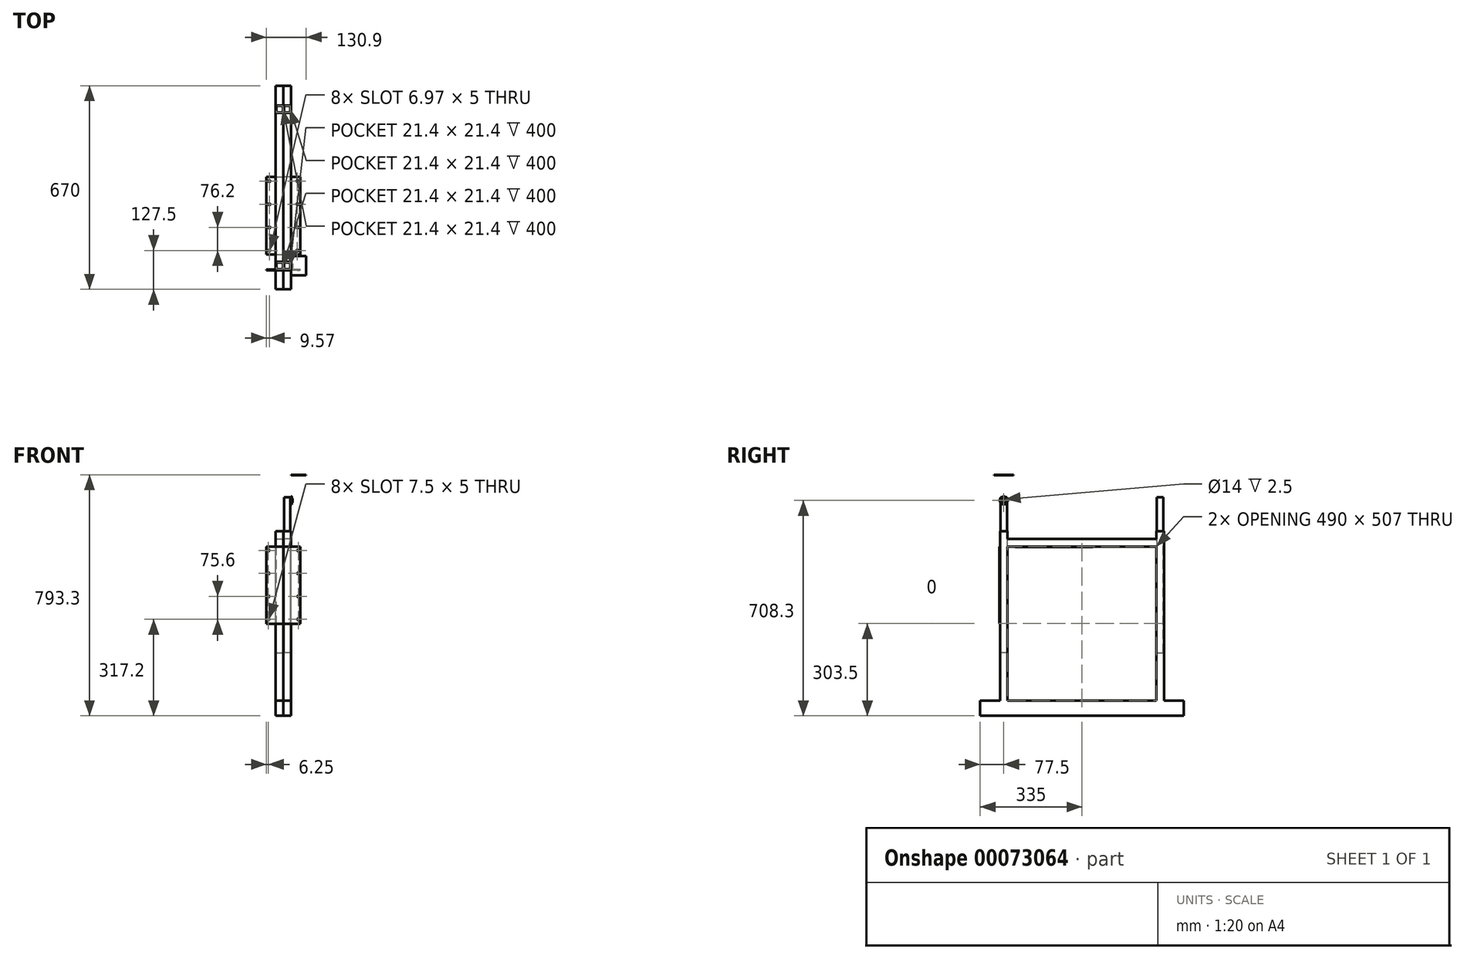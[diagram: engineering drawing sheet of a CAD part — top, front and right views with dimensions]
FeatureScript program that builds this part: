
annotation { "Feature Type Name" : "Feature", "Feature Type Description" : "" }
export const myFeature = defineFeature(function(context is Context, id is Id, definition is map)
    precondition{}
    {
        {
            var Q0;
            Q0=qCreatedBy(makeId("Right.planeOp"),FACE);
            var sketch = newSketch(context, id + "F0", { "sketchPlane" : qUnion([Q0])});
            skLineSegment(sketch, "E0", {"start": v(-335, 0) * mm, "end": v(335, 0) * mm});
            skLineSegment(sketch, "E1.0", {"start": v(-335, 50) * mm, "end": v(335, 50) * mm});
            skLineSegment(sketch, "E2", {"start": v(-335, 50) * mm, "end": v(-335, 0) * mm});
            skLineSegment(sketch, "E3", {"start": v(335, 50) * mm, "end": v(335, 0) * mm});
            skLineSegment(sketch, "E4", {"start": v(270, 50) * mm, "end": v(270, 607) * mm});
            skLineSegment(sketch, "E5.0", {"start": v(245, 50) * mm, "end": v(245, 607) * mm});
            skLineSegment(sketch, "E6", {"start": v(245, 607) * mm, "end": v(270, 607) * mm});
            skLineSegment(sketch, "E7", {"start": v(0, 0) * mm, "end": v(0, 674.81) * mm, "construction": true});
            skPoint(sketch, "E7.endSnap0", {"position": v(0, 50) * mm});
            skLineSegment(sketch, "E8.MirrorCS", {"start": v(-245, 607) * mm, "end": v(-270, 607) * mm});
            skLineSegment(sketch, "E9.MirrorCS", {"start": v(-270, 50) * mm, "end": v(-270, 607) * mm});
            skLineSegment(sketch, "E10.MirrorCS", {"start": v(-245, 50) * mm, "end": v(-245, 607) * mm});
            skLineSegment(sketch, "E11", {"start": v(-245, 557) * mm, "end": v(245, 557) * mm});
            skLineSegment(sketch, "E12.0", {"start": v(-245, 582) * mm, "end": v(245, 582) * mm});
            skLineSegment(sketch, "E13", {"start": v(-220, 557) * mm, "end": v(-220, 555) * mm});
            skLineSegment(sketch, "E14", {"start": v(-220, 555) * mm, "end": v(35, 555) * mm});
            skLineSegment(sketch, "E15", {"start": v(35, 555) * mm, "end": v(35, 557) * mm});
            skLineSegment(sketch, "E16", {"start": v(-270, 557) * mm, "end": v(-272, 557) * mm});
            skLineSegment(sketch, "E17", {"start": v(-272, 557) * mm, "end": v(-272, 302) * mm});
            skLineSegment(sketch, "E18", {"start": v(-272, 302) * mm, "end": v(-270, 302) * mm});
            skSolve(sketch);
        }
        {
            var Q0;
            Q0=makeQuery(id+"F0.imprint","IMPRINT",FACE,{"disambiguationData":[TD([[makeQuery(id+"F0.imprint","IMPRINT",EDGE,{"derivedFrom":sQuery(id+"F0.wireOp",EDGE,"E0")}),1.0]])]});
            var Q1;
            {var subQ5=sQuery(id+"F0.wireOp",EDGE,"E4");Q1=makeQuery(id+"F0.imprint","IMPRINT",FACE,{"disambiguationData":[TD([[makeQuery(id+"F0.imprint","IMPRINT",EDGE,{"derivedFrom":subQ5}),1.0]])]});}
            var Q2;
            {var subQ8=sQuery(id+"F0.wireOp",EDGE,"E8.MirrorCS");Q2=makeQuery(id+"F0.imprint","IMPRINT",FACE,{"disambiguationData":[TD([[makeQuery(id+"F0.imprint","IMPRINT",EDGE,{"derivedFrom":subQ8}),1.0]])]});}
            var Q3;
            {var subQ5=sQuery(id+"F0.wireOp",EDGE,"E12.0");Q3=makeQuery(id+"F0.imprint","IMPRINT",FACE,{"disambiguationData":[TD([[makeQuery(id+"F0.imprint","IMPRINT",EDGE,{"derivedFrom":subQ5}),-1.0]])]});}
            extrude(context, id + "F1", {"entities" : qUnion([Q0, Q1, Q2, Q3]), "depth" : 25 * mm});
        }
        {
            var Q0;
            {var subQ0=sQuery(id+"F0.wireOp",EDGE,"E13");Q0=makeQuery(id+"F0.imprint","IMPRINT",FACE,{"disambiguationData":[TD([[makeQuery(id+"F0.imprint","IMPRINT",EDGE,{"derivedFrom":subQ0}),1.0]])]});}
            var Q1;
            {var subQ0=sQuery(id+"F0.wireOp",EDGE,"E16");Q1=makeQuery(id+"F0.imprint","IMPRINT",FACE,{"disambiguationData":[TD([[makeQuery(id+"F0.imprint","IMPRINT",EDGE,{"derivedFrom":subQ0}),1.0]])]});}
            extrude(context, id + "F2", {"entities" : qUnion([Q0, Q1]), "operationType" : NewBodyOperationType.ADD, "depth" : 55.7 * mm});
        }
        {
            var Q0;
            Q0=makeQuery(id+"F2.opExtrude","SWEPT_FACE",FACE,{"disambiguationData":[OSD([sQuery(id+"F0.wireOp",EDGE,"E11")])]});
            var sketch = newSketch(context, id + "F3", { "sketchPlane" : qUnion([Q0])});
            skArc(sketch, "E19", {"start": v(46.7, -209.96) * mm, "mid": v(49.64, -207.65) * mm, "end": v(47, -205) * mm});
            skArc(sketch, "E20", {"start": v(45.15, -205) * mm, "mid": v(42.64, -207.53) * mm, "end": v(45.2, -210) * mm});
            skLineSegment(sketch, "E21", {"start": v(47.7, -209.94) * mm, "end": v(45.2, -210) * mm});
            skLineSegment(sketch, "E22", {"start": v(47, -205) * mm, "end": v(45.15, -205) * mm});
            skArc(sketch, "E23.0.1.0", {"start": v(46.7, -133.76) * mm, "mid": v(49.64, -131.45) * mm, "end": v(47, -128.8) * mm});
            skArc(sketch, "E23.0.1.1", {"start": v(45.15, -128.8) * mm, "mid": v(42.64, -131.33) * mm, "end": v(45.2, -133.8) * mm});
            skLineSegment(sketch, "E23.0.1.2", {"start": v(47.7, -133.74) * mm, "end": v(45.2, -133.8) * mm});
            skLineSegment(sketch, "E23.0.1.3", {"start": v(47, -128.8) * mm, "end": v(45.15, -128.8) * mm});
            skArc(sketch, "E23.0.2.0", {"start": v(46.7, -57.56) * mm, "mid": v(49.64, -55.25) * mm, "end": v(47, -52.6) * mm});
            skArc(sketch, "E23.0.2.1", {"start": v(45.15, -52.6) * mm, "mid": v(42.64, -55.13) * mm, "end": v(45.2, -57.6) * mm});
            skLineSegment(sketch, "E23.0.2.2", {"start": v(47.7, -57.54) * mm, "end": v(45.2, -57.6) * mm});
            skLineSegment(sketch, "E23.0.2.3", {"start": v(47, -52.6) * mm, "end": v(45.15, -52.6) * mm});
            skArc(sketch, "E23.0.3.0", {"start": v(46.7, 18.64) * mm, "mid": v(49.64, 20.95) * mm, "end": v(47, 23.6) * mm});
            skArc(sketch, "E23.0.3.1", {"start": v(45.15, 23.6) * mm, "mid": v(42.64, 21.07) * mm, "end": v(45.2, 18.6) * mm});
            skLineSegment(sketch, "E23.0.3.2", {"start": v(47.7, 18.66) * mm, "end": v(45.2, 18.6) * mm});
            skLineSegment(sketch, "E23.0.3.3", {"start": v(47, 23.6) * mm, "end": v(45.15, 23.6) * mm});
            skLineSegment(sketch, "E23.direction1", {"start": v(46.7, -209.96) * mm, "end": v(37.88, -209.96) * mm, "construction": true});
            skLineSegment(sketch, "E23.direction2", {"start": v(46.7, -209.96) * mm, "end": v(46.7, -133.76) * mm, "construction": true});
            skSolve(sketch);
        }
        {
            var Q0;
            {var subQ3=sQuery(id+"F3.wireOp",EDGE,"E20");Q0=makeQuery(id+"F3.imprint","IMPRINT",FACE,{"disambiguationData":[TD([[makeQuery(id+"F3.imprint","IMPRINT",EDGE,{"derivedFrom":subQ3}),1.0]])]});}
            var Q1;
            {var subQ3=sQuery(id+"F3.wireOp",EDGE,"E23.0.1.1");Q1=makeQuery(id+"F3.imprint","IMPRINT",FACE,{"disambiguationData":[TD([[makeQuery(id+"F3.imprint","IMPRINT",EDGE,{"derivedFrom":subQ3}),1.0]])]});}
            var Q2;
            {var subQ3=sQuery(id+"F3.wireOp",EDGE,"E23.0.2.1");Q2=makeQuery(id+"F3.imprint","IMPRINT",FACE,{"disambiguationData":[TD([[makeQuery(id+"F3.imprint","IMPRINT",EDGE,{"derivedFrom":subQ3}),1.0]])]});}
            var Q3;
            {var subQ3=sQuery(id+"F3.wireOp",EDGE,"E23.0.3.1");Q3=makeQuery(id+"F3.imprint","IMPRINT",FACE,{"disambiguationData":[TD([[makeQuery(id+"F3.imprint","IMPRINT",EDGE,{"derivedFrom":subQ3}),1.0]])]});}
            extrude(context, id + "F4", {"entities" : qUnion([Q0, Q1, Q2, Q3]), "operationType" : NewBodyOperationType.REMOVE, "oppositeDirection" : true, "depth" : 5 * mm});
        }
        {
            var Q0;
            Q0=makeQuery(id+"F2.opExtrude","SWEPT_FACE",FACE,{"disambiguationData":[OSD([sQuery(id+"F0.wireOp",EDGE,"E17")])]});
            var sketch = newSketch(context, id + "F5", { "sketchPlane" : qUnion([Q0])});
            skArc(sketch, "E24", {"start": v(50.7, 541.5) * mm, "mid": v(53.2, 544) * mm, "end": v(50.7, 546.5) * mm});
            skArc(sketch, "E25", {"start": v(48.28, 546.5) * mm, "mid": v(45.7, 544.04) * mm, "end": v(48.2, 541.5) * mm});
            skLineSegment(sketch, "E26", {"start": v(48.28, 546.5) * mm, "end": v(50.7, 546.5) * mm});
            skLineSegment(sketch, "E27", {"start": v(48.2, 541.5) * mm, "end": v(50.7, 541.5) * mm});
            skArc(sketch, "E28.0.1.0", {"start": v(50.7, 465.9) * mm, "mid": v(53.2, 468.4) * mm, "end": v(50.7, 470.9) * mm});
            skArc(sketch, "E28.0.1.1", {"start": v(48.28, 470.9) * mm, "mid": v(45.7, 468.44) * mm, "end": v(48.2, 465.9) * mm});
            skLineSegment(sketch, "E28.0.1.2", {"start": v(48.28, 470.9) * mm, "end": v(50.7, 470.9) * mm});
            skLineSegment(sketch, "E28.0.1.3", {"start": v(48.2, 465.9) * mm, "end": v(50.7, 465.9) * mm});
            skArc(sketch, "E28.0.2.0", {"start": v(50.7, 390.3) * mm, "mid": v(53.2, 392.8) * mm, "end": v(50.7, 395.3) * mm});
            skArc(sketch, "E28.0.2.1", {"start": v(48.28, 395.3) * mm, "mid": v(45.7, 392.84) * mm, "end": v(48.2, 390.3) * mm});
            skLineSegment(sketch, "E28.0.2.2", {"start": v(48.28, 395.3) * mm, "end": v(50.7, 395.3) * mm});
            skLineSegment(sketch, "E28.0.2.3", {"start": v(48.2, 390.3) * mm, "end": v(50.7, 390.3) * mm});
            skArc(sketch, "E28.0.3.0", {"start": v(50.7, 314.7) * mm, "mid": v(53.2, 317.2) * mm, "end": v(50.7, 319.7) * mm});
            skArc(sketch, "E28.0.3.1", {"start": v(48.28, 319.7) * mm, "mid": v(45.7, 317.24) * mm, "end": v(48.2, 314.7) * mm});
            skLineSegment(sketch, "E28.0.3.2", {"start": v(48.28, 319.7) * mm, "end": v(50.7, 319.7) * mm});
            skLineSegment(sketch, "E28.0.3.3", {"start": v(48.2, 314.7) * mm, "end": v(50.7, 314.7) * mm});
            skLineSegment(sketch, "E28.direction1", {"start": v(50.7, 541.5) * mm, "end": v(71.48, 541.5) * mm, "construction": true});
            skLineSegment(sketch, "E28.direction2", {"start": v(50.7, 541.5) * mm, "end": v(50.7, 465.9) * mm, "construction": true});
            skSolve(sketch);
        }
        {
            var Q0;
            Q0 = qSketchRegion(id + "F5", true);
            extrude(context, id + "F6", {"entities" : qUnion([Q0]), "operationType" : NewBodyOperationType.REMOVE, "oppositeDirection" : true, "depth" : 28.93 * mm});
        }
        {
            var Q0;
            Q0=makeQuery(id+"F1.opExtrude","SWEPT_FACE",FACE,{"disambiguationData":[OSD([sQuery(id+"F0.wireOp",EDGE,"E8.MirrorCS")])]});
            var sketch = newSketch(context, id + "F7", { "sketchPlane" : qUnion([Q0])});
            skLineSegment(sketch, "E29.0", {"start": v(23.2, -246.8) * mm, "end": v(1.8, -246.8) * mm});
            skLineSegment(sketch, "E29.1", {"start": v(23.2, -246.8) * mm, "end": v(23.2, -268.2) * mm});
            skLineSegment(sketch, "E29.2", {"start": v(23.2, -268.2) * mm, "end": v(1.8, -268.2) * mm});
            skLineSegment(sketch, "E29.3", {"start": v(1.8, -246.8) * mm, "end": v(1.8, -268.2) * mm});
            skLineSegment(sketch, "E30.0", {"start": v(23.2, 268.2) * mm, "end": v(1.8, 268.2) * mm});
            skLineSegment(sketch, "E30.1", {"start": v(23.2, 246.8) * mm, "end": v(23.2, 268.2) * mm});
            skLineSegment(sketch, "E30.2", {"start": v(23.2, 246.8) * mm, "end": v(1.8, 246.8) * mm});
            skLineSegment(sketch, "E30.3", {"start": v(1.8, 246.8) * mm, "end": v(1.8, 268.2) * mm});
            skSolve(sketch);
        }
        {
            var Q0;
            Q0=makeQuery(id+"F7.imprint","IMPRINT",FACE,{"disambiguationData":[TD([[makeQuery(id+"F7.imprint","IMPRINT",EDGE,{"derivedFrom":sQuery(id+"F7.wireOp",EDGE,"E30.0")}),1.0]])]});
            var Q1;
            Q1=makeQuery(id+"F7.imprint","IMPRINT",FACE,{"disambiguationData":[TD([[makeQuery(id+"F7.imprint","IMPRINT",EDGE,{"derivedFrom":sQuery(id+"F7.wireOp",EDGE,"E29.0")}),1.0]])]});
            extrude(context, id + "F8", {"entities" : qUnion([Q0, Q1]), "operationType" : NewBodyOperationType.REMOVE, "oppositeDirection" : true, "depth" : 400 * mm});
        }
        {
            var Q0;
            Q0=makeQuery(id+"F8.boolean.opBoolean","COPY",FACE,{"derivedFrom":makeQuery(id+"F8.opExtrude","CAP_FACE",FACE,{"disambiguationData":[OSD([sQuery(id+"F7.wireOp",EDGE,"E29.0"),sQuery(id+"F7.wireOp",EDGE,"E29.1"),sQuery(id+"F7.wireOp",EDGE,"E29.2"),sQuery(id+"F7.wireOp",EDGE,"E29.3")])],"isStart":false})});
            extrude(context, id + "F9", {"entities" : qUnion([Q0]), "depth" : 512 * mm});
        }
        {
            var Q0;
            Q0=makeQuery(id+"F8.boolean.opBoolean","COPY",FACE,{"derivedFrom":makeQuery(id+"F8.opExtrude","CAP_FACE",FACE,{"disambiguationData":[OSD([sQuery(id+"F7.wireOp",EDGE,"E30.0"),sQuery(id+"F7.wireOp",EDGE,"E30.1"),sQuery(id+"F7.wireOp",EDGE,"E30.2"),sQuery(id+"F7.wireOp",EDGE,"E30.3")])],"isStart":false})});
            extrude(context, id + "F10", {"entities" : qUnion([Q0]), "depth" : 512 * mm});
        }
        {
            var Q0;
            Q0=makeQuery(id+"F9.opExtrude","SWEPT_FACE",FACE,{"disambiguationData":[OSD([sQuery(id+"F7.wireOp",EDGE,"E29.1")])]});
            var sketch = newSketch(context, id + "F11", { "sketchPlane" : qUnion([Q0])});
            skCircle(sketch, "E31", {"center": v(-257.5, 708.3) * mm, "radius": 10.7 * mm});
            skCircle(sketch, "E32", {"center": v(-257.5, 708.3) * mm, "radius": 7 * mm});
            skCircle(sketch, "E33", {"center": v(-257.5, 708.3) * mm, "radius": 13 * mm});
            skLineSegment(sketch, "E34", {"start": v(-257.5, 708.3) * mm, "end": v(-257.5, 796.5) * mm, "construction": true});
            skLineSegment(sketch, "E35", {"start": v(-257.5, 793.3) * mm, "end": v(-225.5, 793.3) * mm});
            skLineSegment(sketch, "E36", {"start": v(-225.5, 793.3) * mm, "end": v(-225.5, 738.3) * mm});
            skLineSegment(sketch, "E37", {"start": v(-225.5, 738.3) * mm, "end": v(-246.2, 701.88) * mm});
            skLineSegment(sketch, "E38.0", {"start": v(-257.5, 790.8) * mm, "end": v(-225.5, 790.8) * mm});
            skLineSegment(sketch, "E39.MirrorCS", {"start": v(-257.5, 790.8) * mm, "end": v(-289.5, 790.8) * mm});
            skLineSegment(sketch, "E40.MirrorCS", {"start": v(-257.5, 793.3) * mm, "end": v(-289.5, 793.3) * mm});
            skLineSegment(sketch, "E41.MirrorCS", {"start": v(-289.5, 793.3) * mm, "end": v(-289.5, 738.3) * mm});
            skLineSegment(sketch, "E42.MirrorCS", {"start": v(-289.5, 738.3) * mm, "end": v(-268.8, 701.88) * mm});
            skSolve(sketch);
        }
        {
            var Q0;
            Q0=makeQuery(id+"F11.imprint","IMPRINT",FACE,{"disambiguationData":[TD([[makeQuery(id+"F11.imprint","IMPRINT",EDGE,{"derivedFrom":sQuery(id+"F11.wireOp",EDGE,"E32")}),-1.0]])]});
            var Q1;
            Q1=sQuery(id+"F11.wireOp",EDGE,"E32");
            var Q2;
            Q2=sQuery(id+"F11.wireOp",EDGE,"E31");
            extrude(context, id + "F12", {"entities" : qUnion([Q0]), "surfaceEntities" : qUnion([Q1, Q2]), "depth" : 2.5 * mm});
        }
        {
            var Q0;
            Q0=makeQuery(id+"F11.imprint","IMPRINT",FACE,{"disambiguationData":[TD([[makeQuery(id+"F11.imprint","IMPRINT",EDGE,{"derivedFrom":sQuery(id+"F11.wireOp",EDGE,"E32")}),1.0]])]});
            extrude(context, id + "F13", {"entities" : qUnion([Q0]), "depth" : 7.5 * mm, "hasSecondDirection" : true, "secondDirectionOppositeDirection" : false, "secondDirectionDepth" : 2.5 * mm});
        }
        {
            var Q0;
            Q0=makeQuery(id+"F11.imprint","IMPRINT",FACE,{"disambiguationData":[TD([[makeQuery(id+"F11.imprint","IMPRINT",EDGE,{"derivedFrom":sQuery(id+"F11.wireOp",EDGE,"E32")}),-1.0]])]});
            var Q1;
            {var subQ0=sQuery(id+"F11.wireOp",EDGE,"E31");var subQ1=sQuery(id+"F7.wireOp",EDGE,"E29.1");var subQ2=makeQuery(id+"F9.opExtrude","SWEPT_EDGE",EDGE,{"disambiguationData":[OSD([sQuery(id+"F7.wireOp",EDGE,"E29.0"),subQ1])]});var subQ3=makeQuery(id+"F11.imprint","INTERSECT",VERTEX,{"derivedFrom":[subQ2,subQ0]});Q1=makeQuery(id+"F11.imprint","IMPRINT",FACE,{"disambiguationData":[TD([[makeQuery(id+"F11.imprint","IMPRINT",EDGE,{"disambiguationData":[TD([[subQ3,1.0]])],"derivedFrom":subQ0}),-1.0]])]});}
            var Q2;
            {var subQ0=sQuery(id+"F11.wireOp",EDGE,"E33");var subQ1=makeQuery(id+"F11.imprint","INTERSECT",VERTEX,{"derivedFrom":[subQ0,sQuery(id+"F11.wireOp",EDGE,"E42.MirrorCS")]});Q2=makeQuery(id+"F11.imprint","IMPRINT",FACE,{"disambiguationData":[TD([[makeQuery(id+"F11.imprint","IMPRINT",EDGE,{"disambiguationData":[TD([[subQ1,1.0]])],"derivedFrom":subQ0}),1.0]])]});}
            var Q3;
            {var subQ0=sQuery(id+"F11.wireOp",EDGE,"E33");var subQ1=makeQuery(id+"F11.imprint","INTERSECT",VERTEX,{"derivedFrom":[subQ0,sQuery(id+"F11.wireOp",EDGE,"E37")]});Q3=makeQuery(id+"F11.imprint","IMPRINT",FACE,{"disambiguationData":[TD([[makeQuery(id+"F11.imprint","IMPRINT",EDGE,{"disambiguationData":[TD([[subQ1,1.0]])],"derivedFrom":subQ0}),1.0]])]});}
            var Q4;
            {var subQ0=sQuery(id+"F11.wireOp",EDGE,"E31");var subQ1=sQuery(id+"F7.wireOp",EDGE,"E29.1");var subQ2=makeQuery(id+"F9.opExtrude","CAP_EDGE",EDGE,{"disambiguationData":[OSD([subQ1])],"isStart":false});var subQ3=makeQuery(id+"F11.imprint","INTERSECT",VERTEX,{"derivedFrom":[subQ2,subQ0]});Q4=makeQuery(id+"F11.imprint","IMPRINT",FACE,{"disambiguationData":[TD([[makeQuery(id+"F11.imprint","IMPRINT",EDGE,{"disambiguationData":[TD([[subQ3,1.0]])],"derivedFrom":subQ2}),1.0]])]});}
            var Q5;
            {var subQ0=sQuery(id+"F11.wireOp",EDGE,"E31");var subQ1=sQuery(id+"F7.wireOp",EDGE,"E29.1");var subQ2=makeQuery(id+"F9.opExtrude","CAP_EDGE",EDGE,{"disambiguationData":[OSD([subQ1])],"isStart":false});var subQ3=makeQuery(id+"F11.imprint","INTERSECT",VERTEX,{"derivedFrom":[subQ2,subQ0]});Q5=makeQuery(id+"F11.imprint","IMPRINT",FACE,{"disambiguationData":[TD([[makeQuery(id+"F11.imprint","IMPRINT",EDGE,{"disambiguationData":[TD([[subQ3,-1.0]])],"derivedFrom":subQ2}),1.0]])]});}
            var Q6;
            {var subQ0=sQuery(id+"F11.wireOp",EDGE,"E33");var subQ1=makeQuery(id+"F9.opExtrude","CAP_EDGE",EDGE,{"disambiguationData":[OSD([sQuery(id+"F7.wireOp",EDGE,"E29.1")])],"isStart":false});var subQ2=makeQuery(id+"F11.imprint","INTERSECT",VERTEX,{"disambiguationData":[OD(0.0)],"derivedFrom":[subQ1,subQ0]});Q6=makeQuery(id+"F11.imprint","IMPRINT",FACE,{"disambiguationData":[TD([[makeQuery(id+"F11.imprint","IMPRINT",EDGE,{"disambiguationData":[TD([[subQ2,-1.0]])],"derivedFrom":subQ0}),1.0]])]});}
            var Q7;
            {var subQ3=sQuery(id+"F11.wireOp",EDGE,"E37");Q7=makeQuery(id+"F11.imprint","IMPRINT",FACE,{"disambiguationData":[TD([[makeQuery(id+"F11.imprint","IMPRINT",EDGE,{"derivedFrom":subQ3}),-1.0]])]});}
            var Q8;
            {var subQ0=sQuery(id+"F11.wireOp",EDGE,"E33");var subQ1=sQuery(id+"F7.wireOp",EDGE,"E29.1");var subQ2=makeQuery(id+"F9.opExtrude","CAP_EDGE",EDGE,{"disambiguationData":[OSD([subQ1])],"isStart":false});var subQ3=makeQuery(id+"F11.imprint","INTERSECT",VERTEX,{"disambiguationData":[OD(0.0)],"derivedFrom":[subQ2,subQ0]});Q8=makeQuery(id+"F11.imprint","IMPRINT",FACE,{"disambiguationData":[TD([[makeQuery(id+"F11.imprint","IMPRINT",EDGE,{"disambiguationData":[TD([[subQ3,1.0]])],"derivedFrom":subQ0}),-1.0]])]});}
            var Q9;
            {var subQ0=sQuery(id+"F11.wireOp",EDGE,"E33");var subQ1=sQuery(id+"F7.wireOp",EDGE,"E29.1");var subQ2=makeQuery(id+"F9.opExtrude","CAP_EDGE",EDGE,{"disambiguationData":[OSD([subQ1])],"isStart":false});var subQ3=makeQuery(id+"F11.imprint","INTERSECT",VERTEX,{"disambiguationData":[OD(1.0)],"derivedFrom":[subQ2,subQ0]});Q9=makeQuery(id+"F11.imprint","IMPRINT",FACE,{"disambiguationData":[TD([[makeQuery(id+"F11.imprint","IMPRINT",EDGE,{"disambiguationData":[TD([[subQ3,-1.0]])],"derivedFrom":subQ0}),-1.0]])]});}
            extrude(context, id + "F14", {"entities" : qUnion([Q0, Q1, Q2, Q3, Q4, Q5, Q6, Q7, Q8, Q9]), "operationType" : NewBodyOperationType.ADD, "depth" : 5 * mm, "hasSecondDirection" : true, "secondDirectionOppositeDirection" : false, "secondDirectionDepth" : 2.5 * mm});
        }
        {
            var Q0;
            {var subQ3=sQuery(id+"F11.wireOp",EDGE,"E35");Q0=makeQuery(id+"F11.imprint","IMPRINT",FACE,{"disambiguationData":[TD([[makeQuery(id+"F11.imprint","IMPRINT",EDGE,{"derivedFrom":subQ3}),-1.0]])]});}
            extrude(context, id + "F15", {"entities" : qUnion([Q0]), "operationType" : NewBodyOperationType.ADD, "depth" : 52 * mm, "hasSecondDirection" : true, "secondDirectionOppositeDirection" : false, "secondDirectionDepth" : 2.5 * mm});
        }
        {
            var Q0;
            Q0=makeQuery(id+"F1.opExtrude","SWEPT_BODY",BODY,{"disambiguationData":[OSD([sQuery(id+"F0.wireOp",EDGE,"E0"),sQuery(id+"F0.wireOp",EDGE,"E1.0"),sQuery(id+"F0.wireOp",EDGE,"E2"),sQuery(id+"F0.wireOp",EDGE,"E3"),sQuery(id+"F0.wireOp",EDGE,"E4"),sQuery(id+"F0.wireOp",EDGE,"E5.0"),sQuery(id+"F0.wireOp",EDGE,"E6"),sQuery(id+"F0.wireOp",EDGE,"E8.MirrorCS"),sQuery(id+"F0.wireOp",EDGE,"E9.MirrorCS"),sQuery(id+"F0.wireOp",EDGE,"E10.MirrorCS"),sQuery(id+"F0.wireOp",EDGE,"E11"),sQuery(id+"F0.wireOp",EDGE,"E12.0")])]});
            var Q1;
            Q1=makeQuery(id+"F13.opExtrude","SWEPT_BODY",BODY,{"disambiguationData":[OSD([sQuery(id+"F11.wireOp",EDGE,"E32")])]});
            var Q2;
            Q2=qCreatedBy(makeId("Right.planeOp"),FACE);
            mirror(context, id + "F16", {"entities" : qUnion([Q0, Q1]), "mirrorPlane" : qUnion([Q2])});
        }
    });
